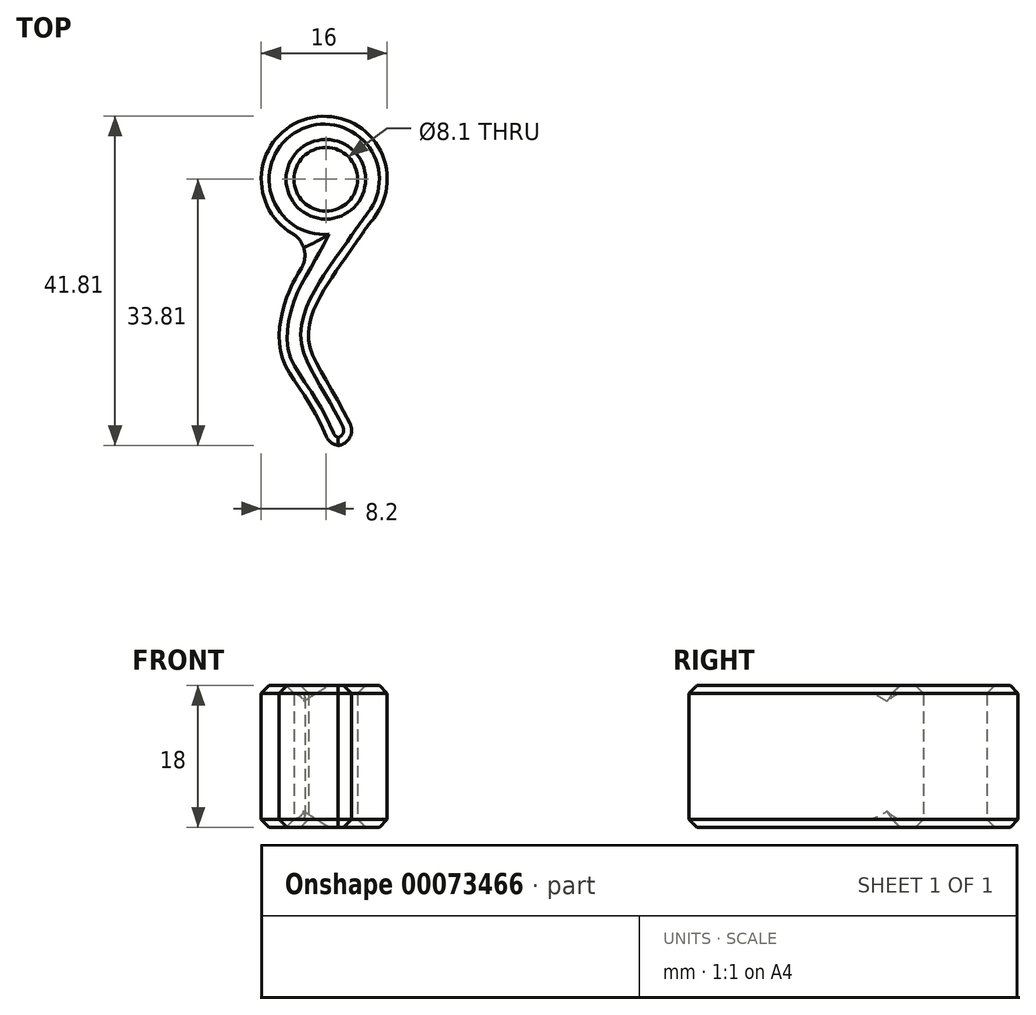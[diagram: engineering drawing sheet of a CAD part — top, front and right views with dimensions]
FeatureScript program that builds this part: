
annotation { "Feature Type Name" : "Feature", "Feature Type Description" : "" }
export const myFeature = defineFeature(function(context is Context, id is Id, definition is map)
    precondition{}
    {
        {
            var Q0;
            Q0=qCreatedBy(makeId("Top.planeOp"),FACE);
            var sketch = newSketch(context, id + "F0", { "sketchPlane" : qUnion([Q0])});
            skCircle(sketch, "E0", {"center": v(0.2, 0) * mm, "radius": 4.05 * mm});
            skCircle(sketch, "E1", {"center": v(0, 0) * mm, "radius": 8 * mm});
            skLineSegment(sketch, "E2", {"start": v(0, 0) * mm, "end": v(0.2, 0) * mm, "construction": true});
            skLineSegment(sketch, "E3", {"start": v(-8, 0) * mm, "end": v(-8, -45.96) * mm, "construction": true});
            skFitSpline(sketch, "E4", {"points": [v(-1.04, -7.93) * mm, v(-4.47, -14.26) * mm, v(-5.55, -21.87) * mm, v(0.69, -33.83) * mm], "startDerivative": vector(-22.72, -42.7) * mm, "endDerivative": vector(15.84, -45.54) * mm});
            skFitSpline(sketch, "E5", {"points": [v(7.46, -2.88) * mm, v(0, -14) * mm, v(-1.96, -20.44) * mm, v(4.51, -33.83) * mm], "startDerivative": vector(-34.68, -53.99) * mm, "endDerivative": vector(20.91, -52.29) * mm});
            skLineSegment(sketch, "E6", {"start": v(0.69, -33.83) * mm, "end": v(4.51, -33.83) * mm});
            skSolve(sketch);
        }
        {
            var Q0;
            Q0 = qSketchRegion(id + "F0", true);
            extrude(context, id + "F1", {"entities" : qUnion([Q0]), "depth" : 18 * mm});
        }
        {
            var Q0;
            Q0=makeQuery(id+"F1.opExtrude","SWEPT_EDGE",EDGE,{"disambiguationData":[OSD([sQuery(id+"F0.wireOp",EDGE,"E5"),sQuery(id+"F0.wireOp",EDGE,"E6")])]});
            var Q1;
            Q1=makeQuery(id+"F1.opExtrude","SWEPT_EDGE",EDGE,{"disambiguationData":[OSD([sQuery(id+"F0.wireOp",EDGE,"E4"),sQuery(id+"F0.wireOp",EDGE,"E6")])]});
            fillet(context, id + "F2", {"entities" : qUnion([Q0, Q1]), "radius" : 1.94 * mm, "tangentPropagation" : true, "allowEdgeOverflow" : false});
        }
        {
            var Q0;
            Q0=makeQuery(id+"F1.opExtrude","SWEPT_EDGE",EDGE,{"disambiguationData":[OSD([sQuery(id+"F0.wireOp",EDGE,"E1"),sQuery(id+"F0.wireOp",EDGE,"E5")])]});
            fillet(context, id + "F3", {"entities" : qUnion([Q0]), "radius" : 53.1 * mm, "tangentPropagation" : true, "allowEdgeOverflow" : false});
        }
        {
            var Q0;
            Q0=makeQuery(id+"F1.opExtrude","CAP_EDGE",EDGE,{"disambiguationData":[OSD([sQuery(id+"F0.wireOp",EDGE,"E4")])],"isStart":true});
            var Q1;
            Q1=makeQuery(id+"F1.opExtrude","CAP_EDGE",EDGE,{"disambiguationData":[OSD([sQuery(id+"F0.wireOp",EDGE,"E1")])],"isStart":true});
            var Q2;
            Q2=makeQuery(id+"F1.opExtrude","CAP_EDGE",EDGE,{"disambiguationData":[OSD([sQuery(id+"F0.wireOp",EDGE,"E1")])],"isStart":false});
            var Q3;
            Q3=makeQuery(id+"F1.opExtrude","CAP_EDGE",EDGE,{"disambiguationData":[OSD([sQuery(id+"F0.wireOp",EDGE,"E4")])],"isStart":false});
            var Q4;
            Q4=makeQuery(id+"F1.opExtrude","CAP_EDGE",EDGE,{"disambiguationData":[OSD([sQuery(id+"F0.wireOp",EDGE,"E0")])],"isStart":false});
            var Q5;
            Q5=makeQuery(id+"F1.opExtrude","CAP_EDGE",EDGE,{"disambiguationData":[OSD([sQuery(id+"F0.wireOp",EDGE,"E0")])],"isStart":true});
            chamfer(context, id + "F4", {"entities" : qUnion([Q0, Q1, Q2, Q3, Q4, Q5]), "width" : 1 * mm, "tangentPropagation" : true});
        }
        {
            var Q0;
            Q0=makeQuery(id+"F1.opExtrude","SWEPT_EDGE",EDGE,{"disambiguationData":[OSD([sQuery(id+"F0.wireOp",EDGE,"E1"),sQuery(id+"F0.wireOp",EDGE,"E4")])]});
            fillet(context, id + "F5", {"entities" : qUnion([Q0]), "radius" : 3.2 * mm, "tangentPropagation" : true, "allowEdgeOverflow" : false});
        }
    });
